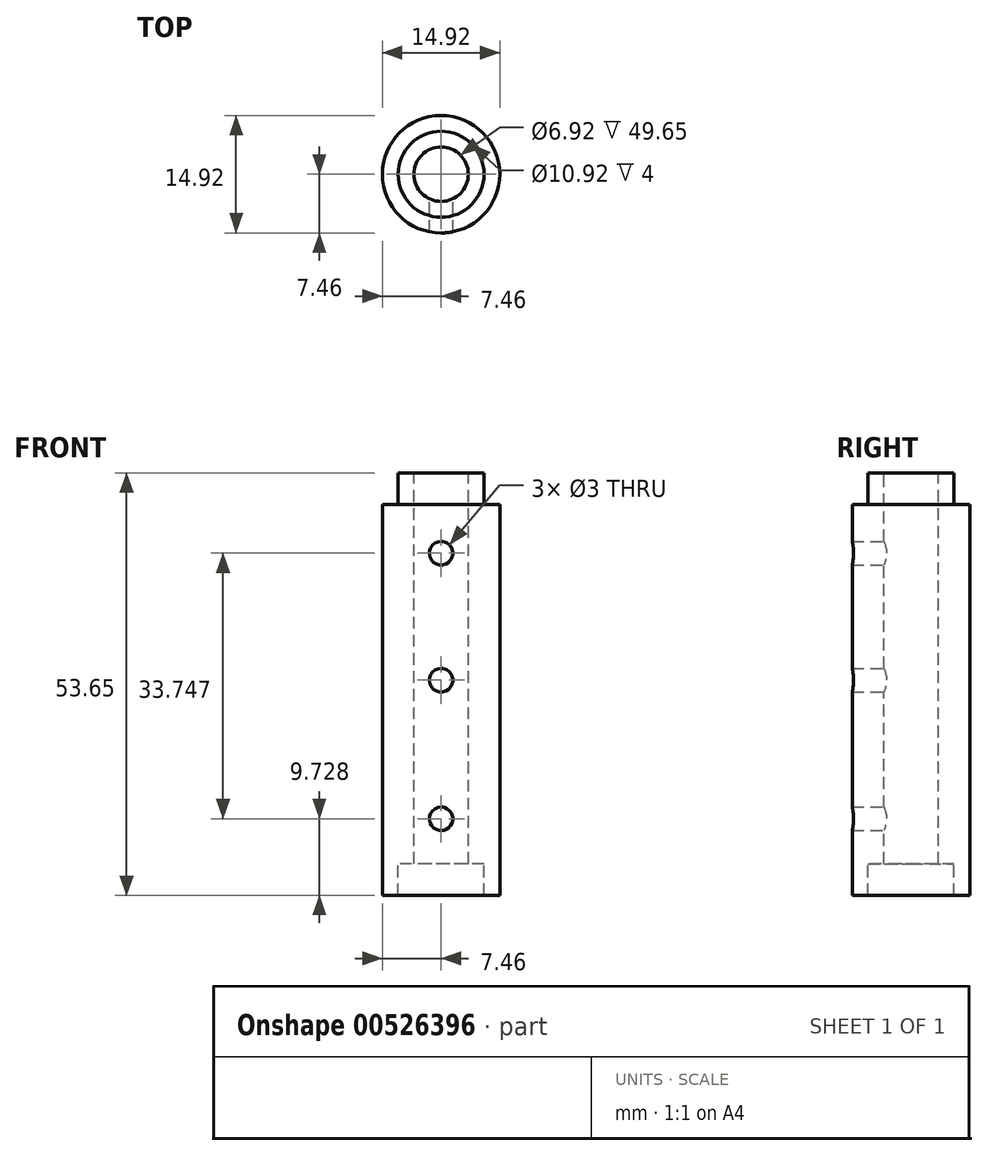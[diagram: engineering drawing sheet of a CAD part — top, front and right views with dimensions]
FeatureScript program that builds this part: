
annotation { "Feature Type Name" : "Feature", "Feature Type Description" : "" }
export const myFeature = defineFeature(function(context is Context, id is Id, definition is map)
    precondition{}
    {
        {
            var Q0;
            Q0=qCreatedBy(makeId("Front.planeOp"),FACE);
            var sketch = newSketch(context, id + "F0", { "sketchPlane" : qUnion([Q0])});
            skLineSegment(sketch, "E0", {"start": v(3.46, 11.82) * mm, "end": v(3.46, 61.47) * mm});
            skLineSegment(sketch, "E1", {"start": v(3.46, 61.47) * mm, "end": v(5.46, 61.47) * mm});
            skLineSegment(sketch, "E2", {"start": v(5.46, 61.47) * mm, "end": v(5.46, 57.47) * mm});
            skLineSegment(sketch, "E3", {"start": v(5.46, 57.47) * mm, "end": v(7.46, 57.47) * mm});
            skLineSegment(sketch, "E4", {"start": v(7.46, 57.47) * mm, "end": v(7.46, 7.82) * mm});
            skLineSegment(sketch, "E5", {"start": v(7.46, 7.82) * mm, "end": v(5.46, 7.82) * mm});
            skLineSegment(sketch, "E6", {"start": v(5.46, 7.82) * mm, "end": v(5.46, 11.82) * mm});
            skLineSegment(sketch, "E7", {"start": v(5.46, 11.82) * mm, "end": v(3.46, 11.82) * mm});
            skLineSegment(sketch, "E8", {"start": v(0, 43.4) * mm, "end": v(0, 22.8) * mm});
            skSolve(sketch);
        }
        {
            var Q0;
            Q0=makeQuery(id+"F0.imprint","IMPRINT",FACE,{"disambiguationData":[TD([[makeQuery(id+"F0.imprint","IMPRINT",EDGE,{"derivedFrom":sQuery(id+"F0.wireOp",EDGE,"E0")}),-1.0]])]});
            var Q1;
            Q1=sQuery(id+"F0.wireOp",EDGE,"E8");
            revolve(context, id + "F1", {"entities" : qUnion([Q0]), "axis" : qUnion([Q1]), "revolveType" : RevolveType.ONE_DIRECTION, "angle" : 360 * degree});
        }
        {
            var Q0;
            Q0=qCreatedBy(makeId("Front.planeOp"),FACE);
            var sketch = newSketch(context, id + "F2", { "sketchPlane" : qUnion([Q0])});
            skPoint(sketch, "E9", {"position": v(0, 51.3) * mm});
            skPoint(sketch, "E10", {"position": v(0, 17.55) * mm});
            skPoint(sketch, "E11", {"position": v(0, 35.16) * mm});
            skSolve(sketch);
        }
        {
            var Q0;
            Q0=sQuery(id+"F2.wireOp",VERTEX,"E9");
            var Q1;
            Q1=sQuery(id+"F2.wireOp",VERTEX,"E11");
            var Q2;
            Q2=sQuery(id+"F2.wireOp",VERTEX,"E10");
            var Q3;
            Q3=makeQuery(id+"F1.opRevolve","SWEPT_BODY",BODY,{"disambiguationData":[OSD([sQuery(id+"F0.wireOp",EDGE,"E0"),sQuery(id+"F0.wireOp",EDGE,"E1"),sQuery(id+"F0.wireOp",EDGE,"E2"),sQuery(id+"F0.wireOp",EDGE,"E3"),sQuery(id+"F0.wireOp",EDGE,"E4"),sQuery(id+"F0.wireOp",EDGE,"E5"),sQuery(id+"F0.wireOp",EDGE,"E6"),sQuery(id+"F0.wireOp",EDGE,"E7")])]});
            hole(context, id + "F3", {"style" : HoleStyle.SIMPLE, "endStyle" : HoleEndStyle.THROUGH, "oppositeDirection" : true, "holeDiameter" : 3 * mm, "isTappedThrough" : true, "tappedDepth" : 12 * mm, "tapClearance" : 3, "locations" : qUnion([Q0, Q1, Q2]), "scope" : qUnion([Q3])});
        }
    });
